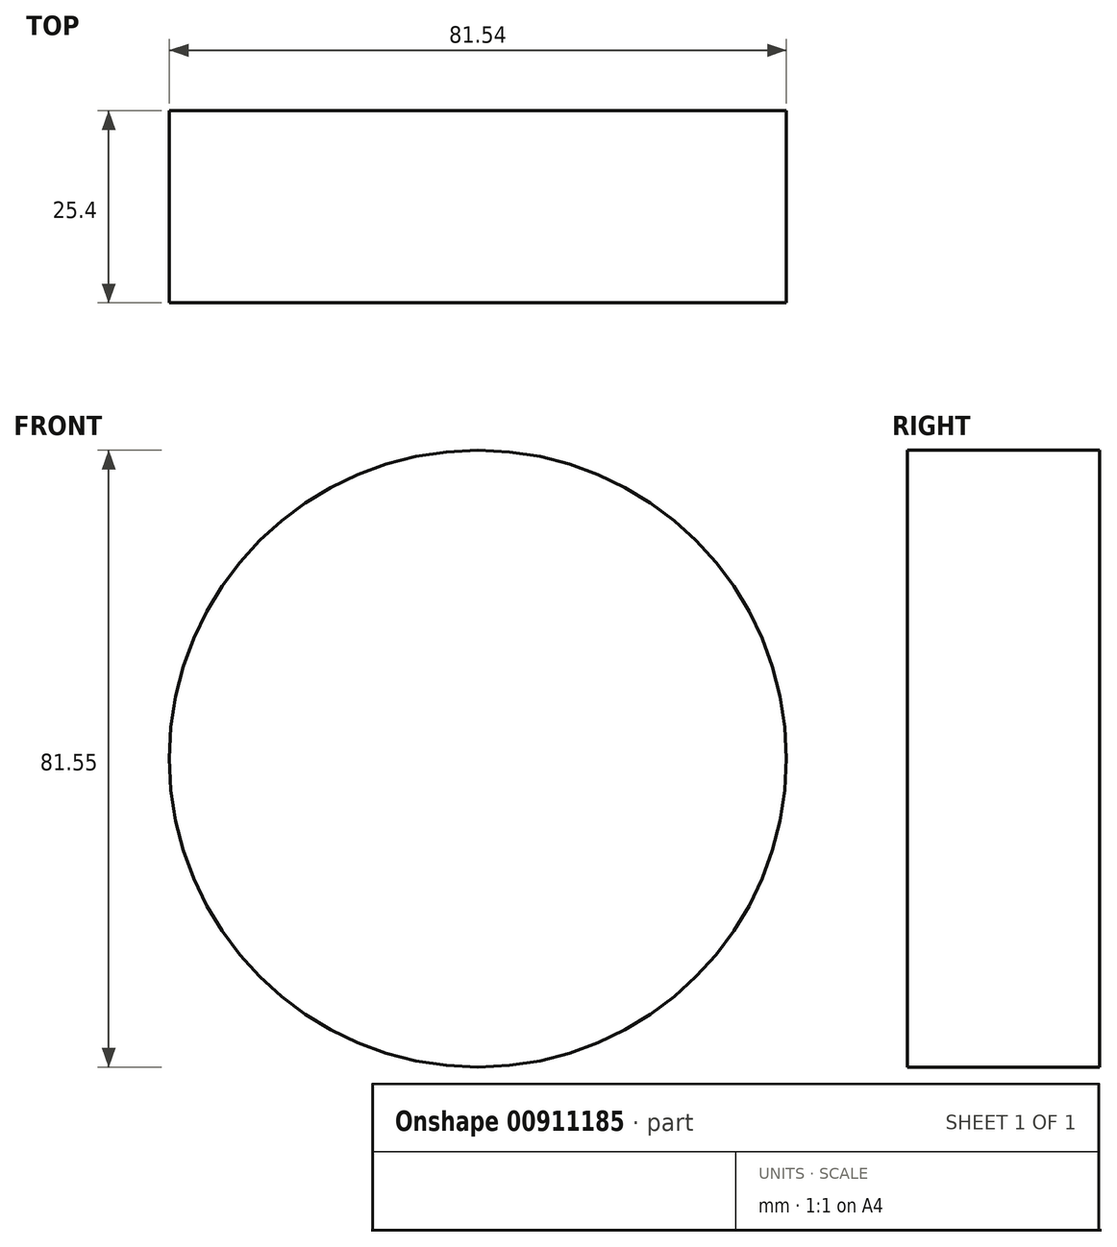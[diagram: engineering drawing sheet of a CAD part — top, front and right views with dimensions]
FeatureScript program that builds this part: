
annotation { "Feature Type Name" : "Feature", "Feature Type Description" : "" }
export const myFeature = defineFeature(function(context is Context, id is Id, definition is map)
    precondition{}
    {
        {
            var Q0;
            Q0=qCreatedBy(makeId("Front.planeOp"),FACE);
            var sketch = newSketch(context, id + "F0", { "sketchPlane" : qUnion([Q0])});
            skCircle(sketch, "E0", {"center": v(0, 1.57) * mm, "radius": 40.77 * mm});
            skSolve(sketch);
        }
        {
            var Q0;
            Q0=makeQuery(id+"F0.imprint","IMPRINT",FACE,{"disambiguationData":[TD([[makeQuery(id+"F0.imprint","IMPRINT",EDGE,{"derivedFrom":sQuery(id+"F0.wireOp",EDGE,"E0")}),1.0]])]});
            extrude(context, id + "F1", {"entities" : qUnion([Q0]), "depth" : 25.4 * mm, "offsetDistance" : 25.4 * mm});
        }
    });
